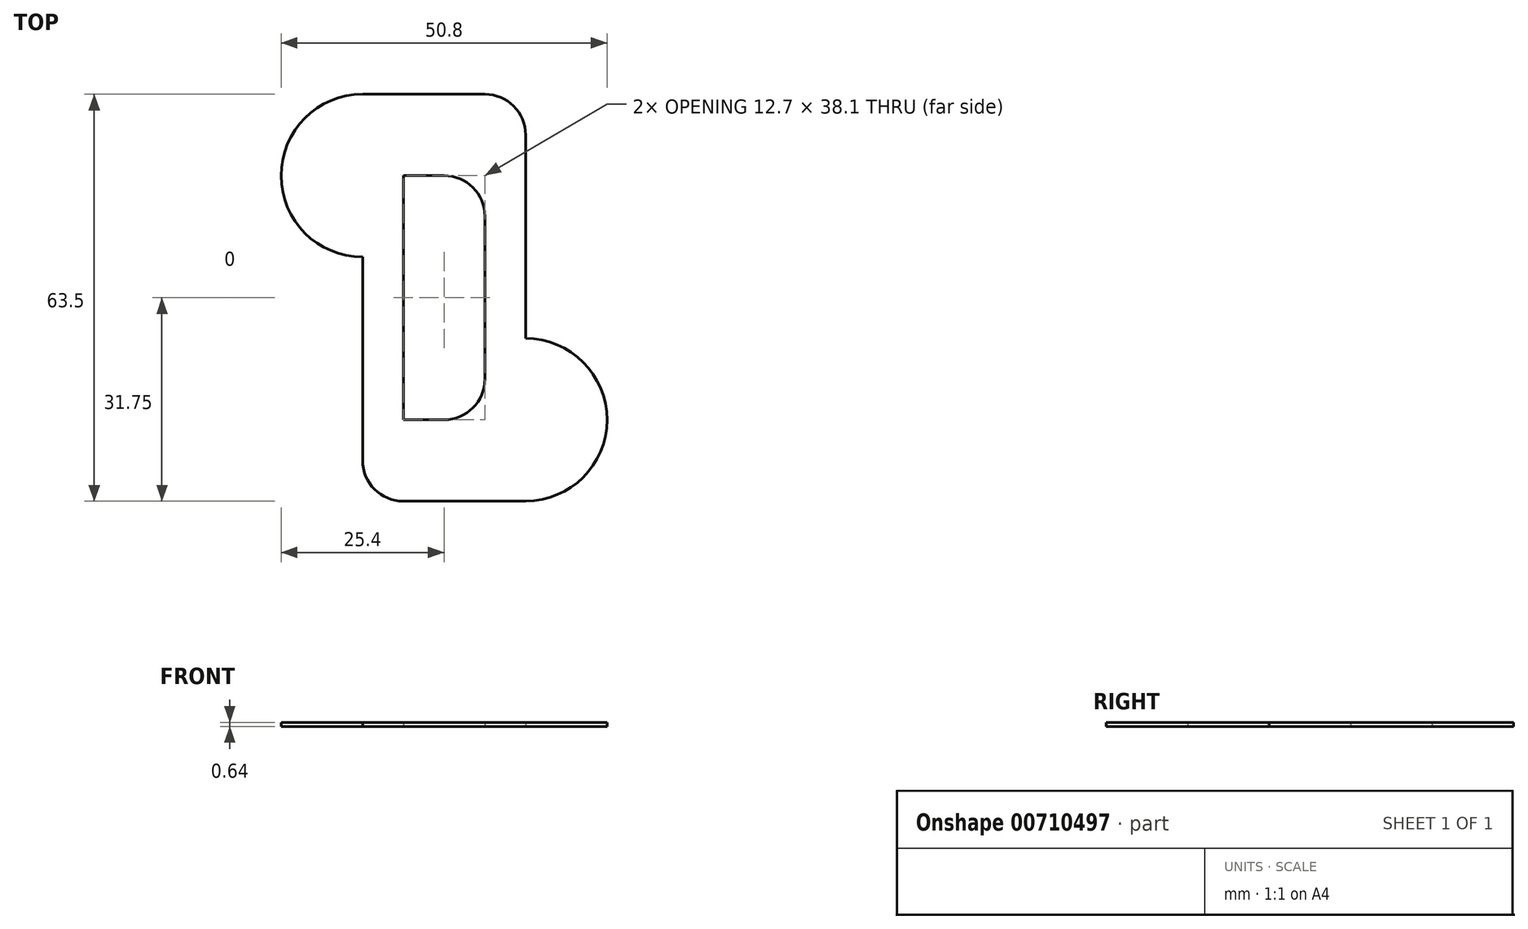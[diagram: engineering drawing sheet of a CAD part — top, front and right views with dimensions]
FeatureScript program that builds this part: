
annotation { "Feature Type Name" : "Feature", "Feature Type Description" : "" }
export const myFeature = defineFeature(function(context is Context, id is Id, definition is map)
    precondition{}
    {
        {
            var Q0;
            Q0=qCreatedBy(makeId("Top.planeOp"),FACE);
            var sketch = newSketch(context, id + "F0", { "sketchPlane" : qUnion([Q0])});
            skLineSegment(sketch, "E0.bottom", {"start": v(12.7, -31.75) * mm, "end": v(-6.35, -31.75) * mm});
            skLineSegment(sketch, "E0.top", {"start": v(6.35, 31.75) * mm, "end": v(-12.7, 31.75) * mm});
            skLineSegment(sketch, "E0.right", {"start": v(-12.7, -25.4) * mm, "end": v(-12.7, 6.35) * mm});
            skPoint(sketch, "E0.middle", {"position": v(0, 0) * mm});
            skArc(sketch, "E1", {"start": v(-12.7, 31.75) * mm, "mid": v(-25.4, 19.05) * mm, "end": v(-12.7, 6.35) * mm});
            skArc(sketch, "E2", {"start": v(12.7, -31.75) * mm, "mid": v(25.4, -19.05) * mm, "end": v(12.7, -6.35) * mm});
            skLineSegment(sketch, "E3.trimOffspring", {"start": v(12.7, -6.35) * mm, "end": v(12.7, 25.4) * mm});
            skPoint(sketch, "E4.start.orphan", {"position": v(-12.7, -19.05) * mm});
            skPoint(sketch, "E5.MirrorCS.end.orphan", {"position": v(12.7, 19.05) * mm});
            skPoint(sketch, "E6.visualSharp", {"position": v(-12.7, -31.75) * mm});
            skArc(sketch, "E6.filletArc", {"start": v(-12.7, -25.4) * mm, "mid": v(-10.84, -29.9) * mm, "end": v(-6.35, -31.75) * mm});
            skPoint(sketch, "E7.visualSharp", {"position": v(12.7, 31.75) * mm});
            skArc(sketch, "E7.filletArc", {"start": v(12.7, 25.4) * mm, "mid": v(10.84, 29.9) * mm, "end": v(6.35, 31.75) * mm});
            skLineSegment(sketch, "E8.bottom", {"start": v(0, -19.05) * mm, "end": v(-6.35, -19.05) * mm});
            skLineSegment(sketch, "E8.top", {"start": v(0, 19.05) * mm, "end": v(-6.35, 19.05) * mm});
            skLineSegment(sketch, "E8.left", {"start": v(6.35, -12.7) * mm, "end": v(6.35, 12.7) * mm});
            skLineSegment(sketch, "E8.right", {"start": v(-6.35, -19.05) * mm, "end": v(-6.35, 19.05) * mm});
            skPoint(sketch, "E9.visualSharp", {"position": v(6.35, 19.05) * mm});
            skArc(sketch, "E9.filletArc", {"start": v(6.35, 12.7) * mm, "mid": v(4.5, 17.2) * mm, "end": v(0, 19.05) * mm});
            skPoint(sketch, "E10.visualSharp", {"position": v(6.35, -19.05) * mm});
            skArc(sketch, "E10.filletArc", {"start": v(0, -19.05) * mm, "mid": v(4.5, -17.2) * mm, "end": v(6.35, -12.7) * mm});
            skSolve(sketch);
        }
        {
            var Q0;
            Q0=qSketchRegion(id+"F0",true);
            extrude(context, id + "F1", {"entities" : qUnion([Q0]), "depth" : 0.64 * mm, "offsetDistance" : 25.4 * mm});
        }
        {
            var Q0;
            Q0=makeQuery(id+"F1.opExtrude","SWEPT_BODY",BODY,{"disambiguationData":[OSD([sQuery(id+"F0.wireOp",EDGE,"E0.bottom"),sQuery(id+"F0.wireOp",EDGE,"E0.top"),sQuery(id+"F0.wireOp",EDGE,"E0.right"),sQuery(id+"F0.wireOp",EDGE,"E1"),sQuery(id+"F0.wireOp",EDGE,"E2"),sQuery(id+"F0.wireOp",EDGE,"E3.trimOffspring"),sQuery(id+"F0.wireOp",EDGE,"E6.filletArc"),sQuery(id+"F0.wireOp",EDGE,"E7.filletArc"),sQuery(id+"F0.wireOp",EDGE,"E8.bottom"),sQuery(id+"F0.wireOp",EDGE,"E8.top"),sQuery(id+"F0.wireOp",EDGE,"E8.left"),sQuery(id+"F0.wireOp",EDGE,"E8.right"),sQuery(id+"F0.wireOp",EDGE,"E9.filletArc"),sQuery(id+"F0.wireOp",EDGE,"E10.filletArc")])]});
            transform(context, id + "F2", {"entities" : qUnion([Q0]), "transformType" : TransformType.TRANSLATION_3D, "dx" : 0 * mm, "dy" : 0 * mm, "dz" : 0 * mm, "makeCopy" : true});
        }
    });
